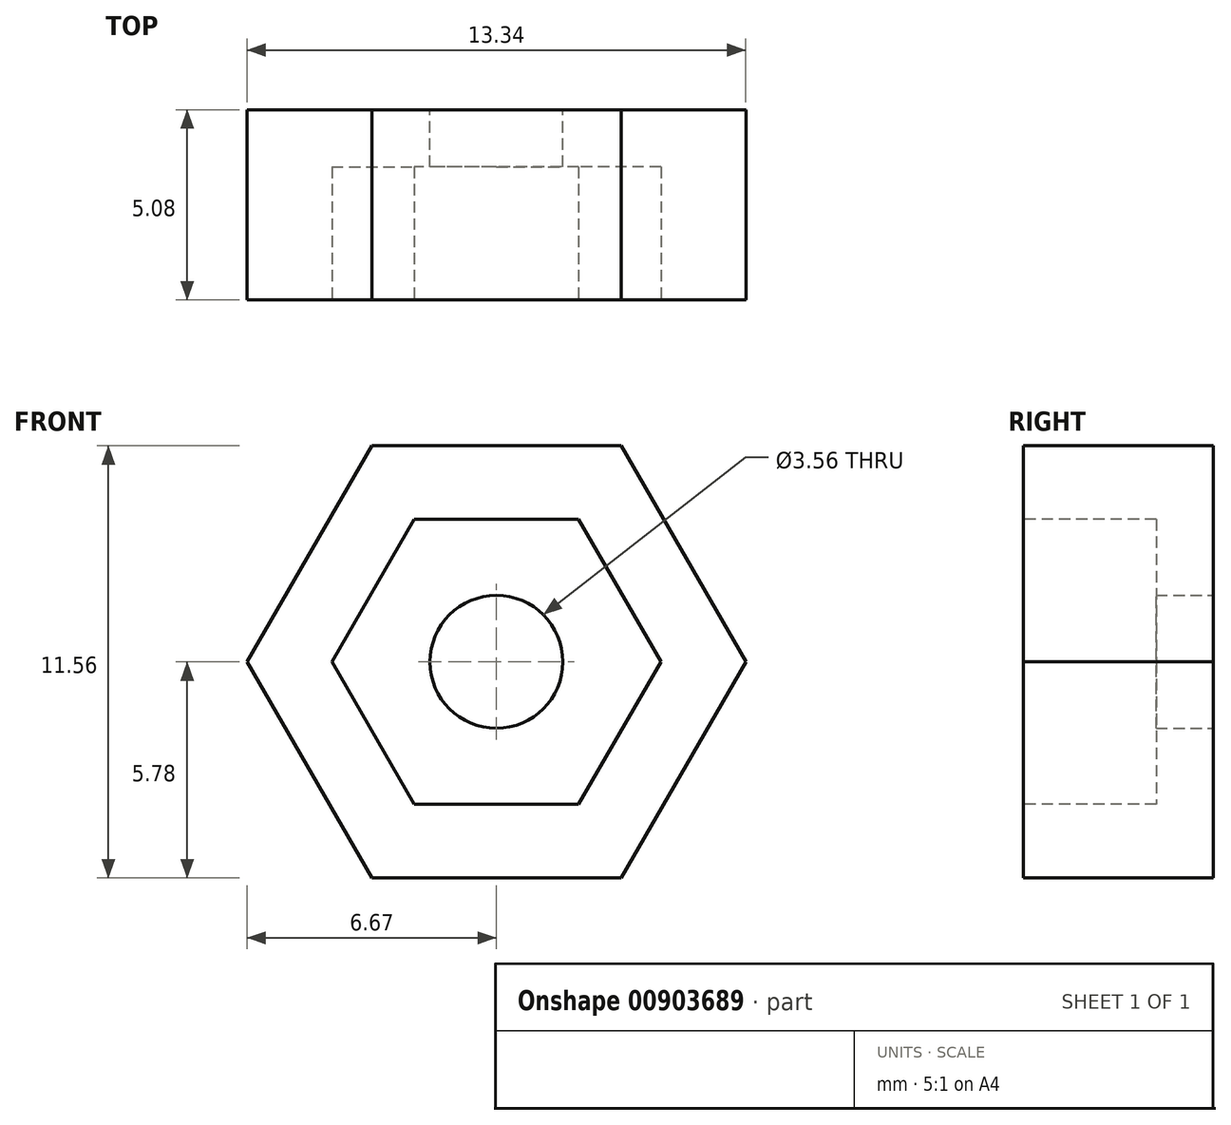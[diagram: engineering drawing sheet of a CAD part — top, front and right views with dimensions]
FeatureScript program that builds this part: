
annotation { "Feature Type Name" : "Feature", "Feature Type Description" : "" }
export const myFeature = defineFeature(function(context is Context, id is Id, definition is map)
    precondition{}
    {
        {
            var Q0;
            Q0=qCreatedBy(makeId("Front.planeOp"),FACE);
            var sketch = newSketch(context, id + "F0", { "sketchPlane" : qUnion([Q0])});
            skCircle(sketch, "E0.cCircle", {"center": v(0, 0) * mm, "radius": 5.78 * mm, "construction": true});
            skLineSegment(sketch, "E0.0", {"start": v(-3.34, 5.78) * mm, "end": v(3.34, 5.78) * mm});
            skLineSegment(sketch, "E0.1", {"start": v(3.34, 5.78) * mm, "end": v(6.67, 0) * mm});
            skLineSegment(sketch, "E0.2", {"start": v(6.67, 0) * mm, "end": v(3.34, -5.78) * mm});
            skLineSegment(sketch, "E0.3", {"start": v(3.34, -5.78) * mm, "end": v(-3.34, -5.78) * mm});
            skLineSegment(sketch, "E0.4", {"start": v(-3.34, -5.78) * mm, "end": v(-6.67, 0) * mm});
            skLineSegment(sketch, "E0.5", {"start": v(-6.67, 0) * mm, "end": v(-3.34, 5.78) * mm});
            skPoint(sketch, "E0.0.midPoint", {"position": v(0, 5.78) * mm});
            skSolve(sketch);
        }
        {
            var Q0;
            Q0 = qSketchRegion(id + "F0", true);
            extrude(context, id + "F1", {"entities" : qUnion([Q0]), "depth" : 5.08 * mm, "offsetDistance" : 25.4 * mm});
        }
        {
            var Q0;
            Q0=makeQuery(id+"F1.opExtrude","CAP_FACE",FACE,{"disambiguationData":[OSD([sQuery(id+"F0.wireOp",EDGE,"E0.0"),sQuery(id+"F0.wireOp",EDGE,"E0.1"),sQuery(id+"F0.wireOp",EDGE,"E0.2"),sQuery(id+"F0.wireOp",EDGE,"E0.3"),sQuery(id+"F0.wireOp",EDGE,"E0.4"),sQuery(id+"F0.wireOp",EDGE,"E0.5")])],"isStart":false});
            var sketch = newSketch(context, id + "F2", { "sketchPlane" : qUnion([Q0])});
            skCircle(sketch, "E1.cCircle", {"center": v(0, 0) * mm, "radius": 3.8 * mm, "construction": true});
            skLineSegment(sketch, "E1.0", {"start": v(2.2, -3.81) * mm, "end": v(-2.2, -3.81) * mm});
            skLineSegment(sketch, "E1.1", {"start": v(-2.2, -3.81) * mm, "end": v(-4.4, 0) * mm});
            skLineSegment(sketch, "E1.2", {"start": v(-4.4, 0) * mm, "end": v(-2.2, 3.8) * mm});
            skLineSegment(sketch, "E1.3", {"start": v(-2.2, 3.8) * mm, "end": v(2.2, 3.81) * mm});
            skLineSegment(sketch, "E1.4", {"start": v(2.2, 3.81) * mm, "end": v(4.4, 0) * mm});
            skLineSegment(sketch, "E1.5", {"start": v(4.4, 0) * mm, "end": v(2.2, -3.81) * mm});
            skPoint(sketch, "E1.0.midPoint", {"position": v(0, -3.8) * mm});
            skSolve(sketch);
        }
        {
            var Q0;
            Q0 = qSketchRegion(id + "F2", true);
            extrude(context, id + "F3", {"entities" : qUnion([Q0]), "operationType" : NewBodyOperationType.REMOVE, "oppositeDirection" : true, "depth" : 3.56 * mm, "offsetDistance" : 25.4 * mm});
        }
        {
            var Q0;
            Q0=makeQuery(id+"F1.opExtrude","CAP_FACE",FACE,{"disambiguationData":[OSD([sQuery(id+"F0.wireOp",EDGE,"E0.0"),sQuery(id+"F0.wireOp",EDGE,"E0.1"),sQuery(id+"F0.wireOp",EDGE,"E0.2"),sQuery(id+"F0.wireOp",EDGE,"E0.3"),sQuery(id+"F0.wireOp",EDGE,"E0.4"),sQuery(id+"F0.wireOp",EDGE,"E0.5")])],"isStart":true});
            var sketch = newSketch(context, id + "F4", { "sketchPlane" : qUnion([Q0])});
            skCircle(sketch, "E2", {"center": v(0, 0) * mm, "radius": 1.78 * mm});
            skSolve(sketch);
        }
        {
            var Q0;
            Q0 = qSketchRegion(id + "F4", true);
            extrude(context, id + "F5", {"entities" : qUnion([Q0]), "operationType" : NewBodyOperationType.REMOVE, "endBound" : BoundingType.THROUGH_ALL, "oppositeDirection" : true, "depth" : 25.4 * mm, "offsetDistance" : 25.4 * mm});
        }
    });
